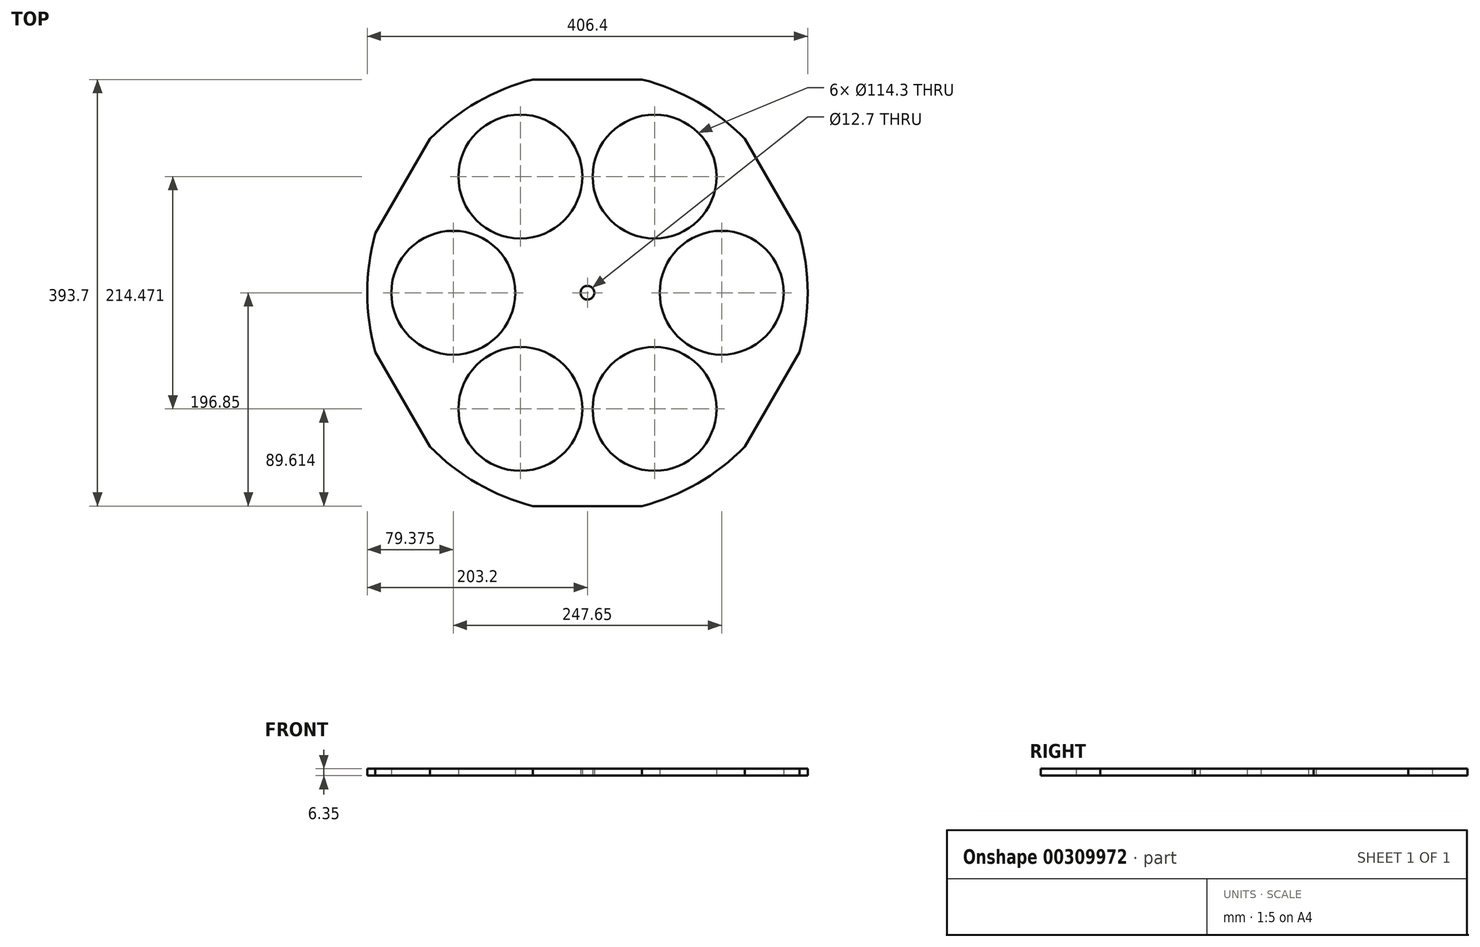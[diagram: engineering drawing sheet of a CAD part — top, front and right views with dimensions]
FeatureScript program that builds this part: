
annotation { "Feature Type Name" : "Feature", "Feature Type Description" : "" }
export const myFeature = defineFeature(function(context is Context, id is Id, definition is map)
    precondition{}
    {
        {
            var Q0;
            Q0=qCreatedBy(makeId("Top.planeOp"),FACE);
            var sketch = newSketch(context, id + "F0", { "sketchPlane" : qUnion([Q0])});
            skCircle(sketch, "E0.cCircle", {"center": v(0, 0) * mm, "radius": 196.85 * mm, "construction": true});
            skLineSegment(sketch, "E0.0", {"start": v(-50.4, 196.85) * mm, "end": v(50.4, 196.85) * mm});
            skLineSegment(sketch, "E0.1", {"start": v(145.28, 142.07) * mm, "end": v(195.68, 54.78) * mm});
            skLineSegment(sketch, "E0.2", {"start": v(195.68, -54.78) * mm, "end": v(145.28, -142.07) * mm});
            skLineSegment(sketch, "E0.3", {"start": v(50.4, -196.85) * mm, "end": v(-50.4, -196.85) * mm});
            skLineSegment(sketch, "E0.4", {"start": v(-145.28, -142.07) * mm, "end": v(-195.68, -54.78) * mm});
            skLineSegment(sketch, "E0.5", {"start": v(-195.68, 54.78) * mm, "end": v(-145.28, 142.07) * mm});
            skPoint(sketch, "E0.0.midPoint", {"position": v(0, 196.85) * mm});
            skArc(sketch, "E1", {"start": v(-195.68, 54.78) * mm, "mid": v(-203.2, 0) * mm, "end": v(-195.68, -54.78) * mm});
            skPoint(sketch, "E2.orphan", {"position": v(-113.65, 196.85) * mm});
            skPoint(sketch, "E3.orphan", {"position": v(-227.3, 0) * mm});
            skArc(sketch, "E4.trimOffspring", {"start": v(-145.28, -142.07) * mm, "mid": v(-101.6, -175.98) * mm, "end": v(-50.4, -196.85) * mm});
            skPoint(sketch, "E5.orphan", {"position": v(-113.65, -196.85) * mm});
            skArc(sketch, "E6.trimOffspring", {"start": v(50.4, -196.85) * mm, "mid": v(101.6, -175.98) * mm, "end": v(145.28, -142.07) * mm});
            skPoint(sketch, "E7.orphan", {"position": v(113.65, -196.85) * mm});
            skArc(sketch, "E8.trimOffspring", {"start": v(195.68, -54.78) * mm, "mid": v(203.2, 0) * mm, "end": v(195.68, 54.78) * mm});
            skPoint(sketch, "E9.orphan", {"position": v(227.3, 0) * mm});
            skArc(sketch, "E10.trimOffspring", {"start": v(145.28, 142.07) * mm, "mid": v(101.6, 175.98) * mm, "end": v(50.4, 196.85) * mm});
            skPoint(sketch, "E11.orphan", {"position": v(113.65, 196.85) * mm});
            skArc(sketch, "E12.trimOffspring", {"start": v(-50.4, 196.85) * mm, "mid": v(-101.6, 175.98) * mm, "end": v(-145.28, 142.07) * mm});
            skCircle(sketch, "E13", {"center": v(-61.91, 107.24) * mm, "radius": 57.15 * mm});
            skLineSegment(sketch, "E14", {"start": v(0, 0) * mm, "end": v(-101.6, 175.98) * mm});
            skCircle(sketch, "E15.1.0", {"center": v(-123.83, 0) * mm, "radius": 57.15 * mm});
            skCircle(sketch, "E15.2.0", {"center": v(-61.91, -107.24) * mm, "radius": 57.15 * mm});
            skCircle(sketch, "E15.3.0", {"center": v(61.91, -107.24) * mm, "radius": 57.15 * mm});
            skCircle(sketch, "E15.4.0", {"center": v(123.83, 0) * mm, "radius": 57.15 * mm});
            skCircle(sketch, "E15.5.0", {"center": v(61.91, 107.24) * mm, "radius": 57.15 * mm});
            skCircle(sketch, "E16", {"center": v(0, 0) * mm, "radius": 6.35 * mm});
            skSolve(sketch);
        }
        {
            var Q0;
            {var subQ1=sQuery(id+"F0.wireOp",EDGE,"E0.0");Q0=makeQuery(id+"F0.imprint","IMPRINT",FACE,{"disambiguationData":[TD([[makeQuery(id+"F0.imprint","IMPRINT",EDGE,{"derivedFrom":subQ1}),-1.0]])]});}
            extrude(context, id + "F1", {"entities" : qUnion([Q0]), "depth" : 6.35 * mm});
        }
    });
